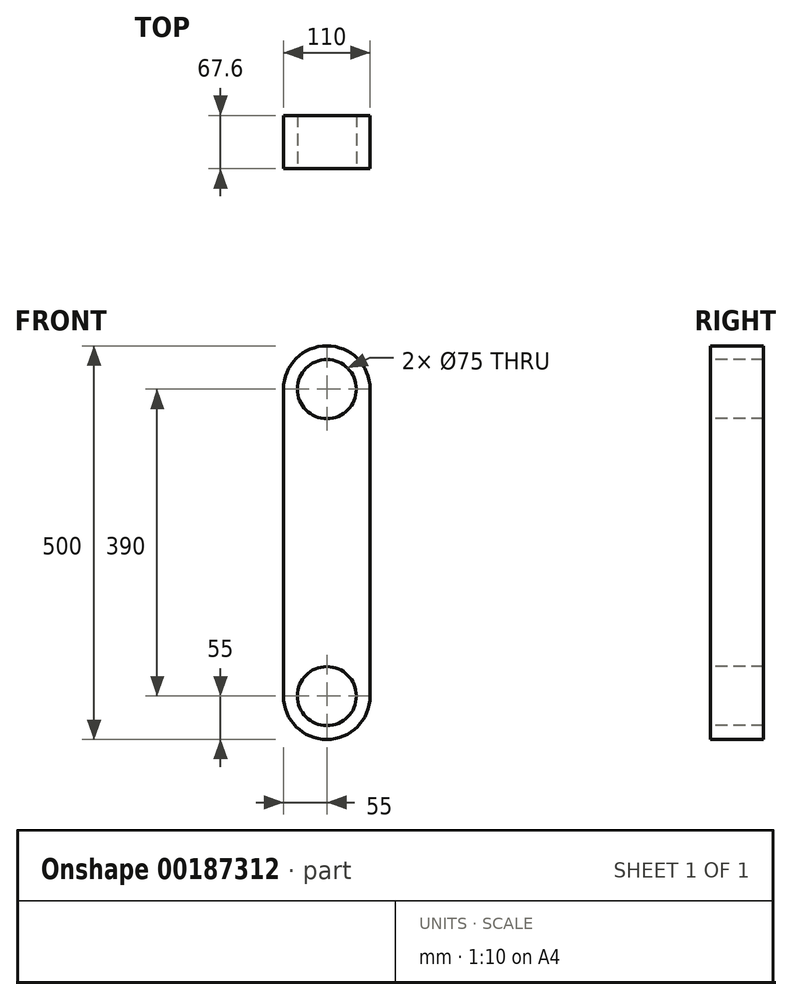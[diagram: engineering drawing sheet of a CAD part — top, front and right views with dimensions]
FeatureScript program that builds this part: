
annotation { "Feature Type Name" : "Feature", "Feature Type Description" : "" }
export const myFeature = defineFeature(function(context is Context, id is Id, definition is map)
    precondition{}
    {
        {
            var Q0;
            Q0=qCreatedBy(makeId("Front.planeOp"),FACE);
            var sketch = newSketch(context, id + "F0", { "sketchPlane" : qUnion([Q0])});
            skLineSegment(sketch, "E0.bottom", {"start": v(0, 250) * mm, "end": v(0, 250) * mm});
            skLineSegment(sketch, "E0.top", {"start": v(0, -250) * mm, "end": v(0, -250) * mm});
            skLineSegment(sketch, "E0.left", {"start": v(55, 195) * mm, "end": v(55, -195) * mm});
            skLineSegment(sketch, "E0.right", {"start": v(-55, 195) * mm, "end": v(-55, -195) * mm});
            skPoint(sketch, "E0.middle", {"position": v(0, 0) * mm});
            skPoint(sketch, "E1.visualSharp", {"position": v(-55, 250) * mm});
            skArc(sketch, "E1.filletArc", {"start": v(0, 250) * mm, "mid": v(-38.9, 233.9) * mm, "end": v(-55, 195) * mm});
            skPoint(sketch, "E2.visualSharp", {"position": v(55, 250) * mm});
            skArc(sketch, "E2.filletArc", {"start": v(55, 195) * mm, "mid": v(38.9, 233.9) * mm, "end": v(0, 250) * mm});
            skPoint(sketch, "E3.visualSharp", {"position": v(-55, -250) * mm});
            skArc(sketch, "E3.filletArc", {"start": v(-55, -195) * mm, "mid": v(-38.9, -233.9) * mm, "end": v(0, -250) * mm});
            skPoint(sketch, "E4.visualSharp", {"position": v(55, -250) * mm});
            skArc(sketch, "E4.filletArc", {"start": v(0, -250) * mm, "mid": v(38.9, -233.9) * mm, "end": v(55, -195) * mm});
            skSolve(sketch);
        }
        {
            var Q0;
            Q0 = qSketchRegion(id + "F0", true);
            extrude(context, id + "F1", {"entities" : qUnion([Q0]), "depth" : 67.6 * mm});
        }
        {
            var Q0;
            Q0=makeQuery(id+"F1.opExtrude","CAP_FACE",FACE,{"disambiguationData":[OSD([sQuery(id+"F0.wireOp",EDGE,"E0.left"),sQuery(id+"F0.wireOp",EDGE,"E0.right"),sQuery(id+"F0.wireOp",EDGE,"E1.filletArc"),sQuery(id+"F0.wireOp",EDGE,"E2.filletArc"),sQuery(id+"F0.wireOp",EDGE,"E3.filletArc"),sQuery(id+"F0.wireOp",EDGE,"E4.filletArc")])],"isStart":false});
            var sketch = newSketch(context, id + "F2", { "sketchPlane" : qUnion([Q0])});
            skCircle(sketch, "E5", {"center": v(0, 195) * mm, "radius": 37.5 * mm});
            skCircle(sketch, "E6.MirrorC", {"center": v(0, -195) * mm, "radius": 37.5 * mm});
            skSolve(sketch);
        }
        {
            var Q0;
            Q0 = qSketchRegion(id + "F2", true);
            var Q1;
            Q1=makeQuery(id+"F1.opExtrude","CAP_FACE",FACE,{"disambiguationData":[OSD([sQuery(id+"F0.wireOp",EDGE,"E0.left"),sQuery(id+"F0.wireOp",EDGE,"E0.right"),sQuery(id+"F0.wireOp",EDGE,"E1.filletArc"),sQuery(id+"F0.wireOp",EDGE,"E2.filletArc"),sQuery(id+"F0.wireOp",EDGE,"E3.filletArc"),sQuery(id+"F0.wireOp",EDGE,"E4.filletArc")])],"isStart":true});
            extrude(context, id + "F3", {"entities" : qUnion([Q0]), "operationType" : NewBodyOperationType.REMOVE, "endBound" : BoundingType.UP_TO_SURFACE, "oppositeDirection" : true, "endBoundEntityFace" : qUnion([Q1]), "depth" : 25 * mm});
        }
    });
